annotation { "Feature Type Name" : "Feature", "Feature Type Description" : "" }
export const myFeature = defineFeature(function(context is Context, id is Id, definition is map)
    precondition{}
    {
        {
            var Q0;
            Q0=qCreatedBy(makeId("Top.planeOp"),FACE);
            var sketch = newSketch(context, id + "F0", { "sketchPlane" : qUnion([Q0])});
            skCircle(sketch, "E0", {"center": v(0, 0) * mm, "radius": 50 * mm});
            skSolve(sketch);
        }
        {
            var Q0;
            Q0=makeQuery(id+"F0.imprint","IMPRINT",FACE,{"disambiguationData":[TD([[makeQuery(id+"F0.imprint","IMPRINT",EDGE,{"derivedFrom":sQuery(id+"F0.wireOp",EDGE,"E0")}),1.0]])]});
            extrude(context, id + "F1", {"entities" : qUnion([Q0]), "depth" : 10 * mm});
        }
        {
            var Q0;
            Q0=makeQuery(id+"F1.opExtrude","SWEPT_FACE",FACE,{"disambiguationData":[OSD([sQuery(id+"F0.wireOp",EDGE,"E0")])]});
            var Q1;
            Q1=makeQuery(id+"F1.opExtrude","CAP_FACE",FACE,{"disambiguationData":[OSD([sQuery(id+"F0.wireOp",EDGE,"E0")])],"isStart":true});
            fillet(context, id + "F2", {"entities" : qUnion([Q0, Q1]), "radius" : 2 * mm, "tangentPropagation" : true, "allowEdgeOverflow" : false});
        }
        {
            var Q0;
            Q0=qCreatedBy(makeId("Top.planeOp"),FACE);
            var sketch = newSketch(context, id + "F3", { "sketchPlane" : qUnion([Q0])});
            skArc(sketch, "E1", {"start": v(45.47, 63.4) * mm, "mid": v(37.47, 55.4) * mm, "end": v(45.47, 47.4) * mm});
            skLineSegment(sketch, "E2", {"start": v(45.47, 55.4) * mm, "end": v(45.47, 63.4) * mm});
            skLineSegment(sketch, "E3", {"start": v(45.47, 63.4) * mm, "end": v(45.47, 47.4) * mm});
            skSolve(sketch);
        }
        {
            var Q0;
            {var subQ0=sQuery(id+"F3.wireOp",EDGE,"E1");Q0=makeQuery(id+"F3.imprint","IMPRINT",FACE,{"disambiguationData":[TD([[makeQuery(id+"F3.imprint","IMPRINT",EDGE,{"derivedFrom":subQ0}),1.0]])]});}
            var Q1;
            Q1=sQuery(id+"F3.wireOp",EDGE,"E3");
            revolve(context, id + "F4", {"entities" : qUnion([Q0]), "axis" : qUnion([Q1]), "revolveType" : RevolveType.FULL});
        }
        {
            var Q0;
            Q0=makeQuery(id+"F4.opRevolve","SWEPT_BODY",BODY,{"disambiguationData":[OSD([sQuery(id+"F3.wireOp",EDGE,"E1"),sQuery(id+"F3.wireOp",EDGE,"E3")])]});
            var Q1;
            Q1=makeQuery(id+"F4.opRevolve","SWEPT_FACE",FACE,{"disambiguationData":[OSD([sQuery(id+"F3.wireOp",EDGE,"E1")])]});
            transform(context, id + "F5", {"entities" : qUnion([Q0]), "transformType" : TransformType.TRANSLATION_3D, "dx" : -7.8 * mm, "dy" : 33.7 * mm, "dz" : 0 * mm, "makeCopy" : false});
        }
        {
            var Q0;
            Q0=qCreatedBy(makeId("Front.planeOp"),FACE);
            var sketch = newSketch(context, id + "F6", { "sketchPlane" : qUnion([Q0])});
            skLineSegment(sketch, "E4", {"start": v(0, 17.62) * mm, "end": v(49.25, 17.62) * mm});
            skLineSegment(sketch, "E5", {"start": v(49.25, 17.62) * mm, "end": v(23.09, 115.37) * mm});
            skLineSegment(sketch, "E6", {"start": v(23.09, 115.37) * mm, "end": v(0, 115.37) * mm});
            skLineSegment(sketch, "E7", {"start": v(0, 115.37) * mm, "end": v(0, 17.62) * mm});
            skLineSegment(sketch, "E8", {"start": v(44.4, 17.62) * mm, "end": v(18.23, 115.37) * mm});
            skSolve(sketch);
        }
        {
            var Q0;
            {var subQ0=sQuery(id+"F6.wireOp",EDGE,"E5");Q0=makeQuery(id+"F6.imprint","IMPRINT",FACE,{"disambiguationData":[TD([[makeQuery(id+"F6.imprint","IMPRINT",EDGE,{"derivedFrom":subQ0}),1.0]])]});}
            var Q1;
            Q1=sQuery(id+"F6.wireOp",EDGE,"E7");
            revolve(context, id + "F7", {"entities" : qUnion([Q0]), "axis" : qUnion([Q1]), "revolveType" : RevolveType.FULL});
        }
        {
            var Q0;
            Q0=makeQuery(id+"F7.opRevolve","SWEPT_BODY",BODY,{"disambiguationData":[OSD([sQuery(id+"F6.wireOp",EDGE,"E4"),sQuery(id+"F6.wireOp",EDGE,"E5"),sQuery(id+"F6.wireOp",EDGE,"E6"),sQuery(id+"F6.wireOp",EDGE,"E8")])]});
            transform(context, id + "F8", {"entities" : qUnion([Q0]), "transformType" : TransformType.TRANSLATION_3D, "dx" : 0 * mm, "dy" : 0 * mm, "dz" : -8.2 * mm, "makeCopy" : false});
        }
        {
            var Q0;
            Q0=makeQuery(id+"F4.opRevolve","SWEPT_BODY",BODY,{"disambiguationData":[OSD([sQuery(id+"F3.wireOp",EDGE,"E1"),sQuery(id+"F3.wireOp",EDGE,"E3")])]});
            transform(context, id + "F9", {"entities" : qUnion([Q0]), "transformType" : TransformType.TRANSLATION_3D, "dx" : -73 * mm, "dy" : 0 * mm, "dz" : 0 * mm, "makeCopy" : true});
        }
        {
            var Q0;
            Q0=makeQuery(id+"F9.opPattern","COPY",BODY,{"derivedFrom":makeQuery(id+"F4.opRevolve","SWEPT_BODY",BODY,{"disambiguationData":[OSD([sQuery(id+"F3.wireOp",EDGE,"E1"),sQuery(id+"F3.wireOp",EDGE,"E3")])]}),"instanceName":"1"});
            transform(context, id + "F10", {"entities" : qUnion([Q0]), "transformType" : TransformType.TRANSLATION_3D, "dx" : 62 * mm, "dy" : 46 * mm, "dz" : 0 * mm, "makeCopy" : true});
        }
        {
            var Q0;
            Q0=makeQuery(id+"F9.opPattern","COPY",BODY,{"derivedFrom":makeQuery(id+"F4.opRevolve","SWEPT_BODY",BODY,{"disambiguationData":[OSD([sQuery(id+"F3.wireOp",EDGE,"E1"),sQuery(id+"F3.wireOp",EDGE,"E3")])]}),"instanceName":"1"});
            var Q1;
            Q1=makeQuery(id+"F4.opRevolve","SWEPT_BODY",BODY,{"disambiguationData":[OSD([sQuery(id+"F3.wireOp",EDGE,"E1"),sQuery(id+"F3.wireOp",EDGE,"E3")])]});
            transform(context, id + "F11", {"entities" : qUnion([Q0, Q1]), "transformType" : TransformType.TRANSLATION_3D, "dx" : 29 * mm, "dy" : -104 * mm, "dz" : 31 * mm, "makeCopy" : false});
        }
        {
            var Q0;
            Q0=makeQuery(id+"F4.opRevolve","SWEPT_BODY",BODY,{"disambiguationData":[OSD([sQuery(id+"F3.wireOp",EDGE,"E1"),sQuery(id+"F3.wireOp",EDGE,"E3")])]});
            transform(context, id + "F12", {"entities" : qUnion([Q0]), "transformType" : TransformType.TRANSLATION_3D, "dx" : -53 * mm, "dy" : 4 * mm, "dz" : 25 * mm, "makeCopy" : false});
        }
        {
            var Q0;
            Q0=makeQuery(id+"F10.opPattern","COPY",BODY,{"derivedFrom":makeQuery(id+"F9.opPattern","COPY",BODY,{"derivedFrom":makeQuery(id+"F4.opRevolve","SWEPT_BODY",BODY,{"disambiguationData":[OSD([sQuery(id+"F3.wireOp",EDGE,"E1"),sQuery(id+"F3.wireOp",EDGE,"E3")])]}),"instanceName":"1"}),"instanceName":"1"});
            transform(context, id + "F13", {"entities" : qUnion([Q0]), "transformType" : TransformType.TRANSLATION_3D, "dx" : -36 * mm, "dy" : -122 * mm, "dz" : 77 * mm, "makeCopy" : false});
        }
        {
            var Q0;
            Q0=qCreatedBy(makeId("Front.planeOp"),FACE);
            var sketch = newSketch(context, id + "F14", { "sketchPlane" : qUnion([Q0])});
            skText(sketch, "E9", { "text": "Tutorial", "fontName": "OpenSans-Regular.ttf"});
            skText(sketch, "E10", { "text": "Kinematics", "fontName": "OpenSans-Regular.ttf"});
            skText(sketch, "E11", { "text": "Particle Physics", "fontName": "OpenSans-Regular.ttf"});
            const initialGuessF14  = {"E9": [-0.02165, 0.0885, 1, 0, 0.00375], "E10": [0.00114, 0.0665, 1, 0, 0.004], "E11": [-0.0259, 0.04173, 1, 0, 0.00358]};
            skSetInitialGuess(sketch, initialGuessF14);
            skSolve(sketch);
        }
        {
            var Q0;
            Q0 = qSketchRegion(id + "F14", true);
            extrude(context, id + "F15", {"entities" : qUnion([Q0]), "depth" : 2 * mm});
        }
        {
            var Q0;
            Q0=makeQuery(id+"F15.opExtrude","SWEPT_BODY",BODY,{"disambiguationData":[OSD([sQuery(id+"F14.wireOp",EDGE,"E9.sketch_text.stroke-0"),sQuery(id+"F14.wireOp",EDGE,"E9.sketch_text.stroke-1"),sQuery(id+"F14.wireOp",EDGE,"E9.sketch_text.stroke-2"),sQuery(id+"F14.wireOp",EDGE,"E9.sketch_text.stroke-3"),sQuery(id+"F14.wireOp",EDGE,"E9.sketch_text.stroke-4"),sQuery(id+"F14.wireOp",EDGE,"E9.sketch_text.stroke-5"),sQuery(id+"F14.wireOp",EDGE,"E9.sketch_text.stroke-6"),sQuery(id+"F14.wireOp",EDGE,"E9.sketch_text.stroke-7"),sQuery(id+"F14.wireOp",EDGE,"E9.sketch_text.stroke-8"),sQuery(id+"F14.wireOp",EDGE,"E9.sketch_text.stroke-9"),sQuery(id+"F14.wireOp",EDGE,"E9.sketch_text.stroke-10"),sQuery(id+"F14.wireOp",EDGE,"E9.sketch_text.stroke-11"),sQuery(id+"F14.wireOp",EDGE,"E9.sketch_text.stroke-12")])]});
            var Q1;
            Q1=makeQuery(id+"F15.opExtrude","SWEPT_BODY",BODY,{"disambiguationData":[OSD([sQuery(id+"F14.wireOp",EDGE,"E9.sketch_text.stroke-13"),sQuery(id+"F14.wireOp",EDGE,"E9.sketch_text.stroke-14"),sQuery(id+"F14.wireOp",EDGE,"E9.sketch_text.stroke-15"),sQuery(id+"F14.wireOp",EDGE,"E9.sketch_text.stroke-16"),sQuery(id+"F14.wireOp",EDGE,"E9.sketch_text.stroke-17"),sQuery(id+"F14.wireOp",EDGE,"E9.sketch_text.stroke-18"),sQuery(id+"F14.wireOp",EDGE,"E9.sketch_text.stroke-19"),sQuery(id+"F14.wireOp",EDGE,"E9.sketch_text.stroke-20"),sQuery(id+"F14.wireOp",EDGE,"E9.sketch_text.stroke-21"),sQuery(id+"F14.wireOp",EDGE,"E9.sketch_text.stroke-22"),sQuery(id+"F14.wireOp",EDGE,"E9.sketch_text.stroke-23"),sQuery(id+"F14.wireOp",EDGE,"E9.sketch_text.stroke-24"),sQuery(id+"F14.wireOp",EDGE,"E9.sketch_text.stroke-25"),sQuery(id+"F14.wireOp",EDGE,"E9.sketch_text.stroke-26"),sQuery(id+"F14.wireOp",EDGE,"E9.sketch_text.stroke-27"),sQuery(id+"F14.wireOp",EDGE,"E9.sketch_text.stroke-28"),sQuery(id+"F14.wireOp",EDGE,"E9.sketch_text.stroke-29"),sQuery(id+"F14.wireOp",EDGE,"E9.sketch_text.stroke-30"),sQuery(id+"F14.wireOp",EDGE,"E9.sketch_text.stroke-31"),sQuery(id+"F14.wireOp",EDGE,"E9.sketch_text.stroke-32"),sQuery(id+"F14.wireOp",EDGE,"E9.sketch_text.stroke-33"),sQuery(id+"F14.wireOp",EDGE,"E9.sketch_text.stroke-34"),sQuery(id+"F14.wireOp",EDGE,"E9.sketch_text.stroke-35"),sQuery(id+"F14.wireOp",EDGE,"E9.sketch_text.stroke-36"),sQuery(id+"F14.wireOp",EDGE,"E9.sketch_text.stroke-37")])]});
            var Q2;
            Q2=makeQuery(id+"F15.opExtrude","SWEPT_BODY",BODY,{"disambiguationData":[OSD([sQuery(id+"F14.wireOp",EDGE,"E9.sketch_text.stroke-38"),sQuery(id+"F14.wireOp",EDGE,"E9.sketch_text.stroke-39"),sQuery(id+"F14.wireOp",EDGE,"E9.sketch_text.stroke-40"),sQuery(id+"F14.wireOp",EDGE,"E9.sketch_text.stroke-41"),sQuery(id+"F14.wireOp",EDGE,"E9.sketch_text.stroke-42"),sQuery(id+"F14.wireOp",EDGE,"E9.sketch_text.stroke-43"),sQuery(id+"F14.wireOp",EDGE,"E9.sketch_text.stroke-44"),sQuery(id+"F14.wireOp",EDGE,"E9.sketch_text.stroke-45"),sQuery(id+"F14.wireOp",EDGE,"E9.sketch_text.stroke-46"),sQuery(id+"F14.wireOp",EDGE,"E9.sketch_text.stroke-47"),sQuery(id+"F14.wireOp",EDGE,"E9.sketch_text.stroke-48"),sQuery(id+"F14.wireOp",EDGE,"E9.sketch_text.stroke-49"),sQuery(id+"F14.wireOp",EDGE,"E9.sketch_text.stroke-50"),sQuery(id+"F14.wireOp",EDGE,"E9.sketch_text.stroke-51"),sQuery(id+"F14.wireOp",EDGE,"E9.sketch_text.stroke-52"),sQuery(id+"F14.wireOp",EDGE,"E9.sketch_text.stroke-53"),sQuery(id+"F14.wireOp",EDGE,"E9.sketch_text.stroke-54"),sQuery(id+"F14.wireOp",EDGE,"E9.sketch_text.stroke-55"),sQuery(id+"F14.wireOp",EDGE,"E9.sketch_text.stroke-56")])]});
            var Q3;
            Q3=makeQuery(id+"F15.opExtrude","SWEPT_BODY",BODY,{"disambiguationData":[OSD([sQuery(id+"F14.wireOp",EDGE,"E9.sketch_text.stroke-57"),sQuery(id+"F14.wireOp",EDGE,"E9.sketch_text.stroke-58"),sQuery(id+"F14.wireOp",EDGE,"E9.sketch_text.stroke-59"),sQuery(id+"F14.wireOp",EDGE,"E9.sketch_text.stroke-60"),sQuery(id+"F14.wireOp",EDGE,"E9.sketch_text.stroke-61"),sQuery(id+"F14.wireOp",EDGE,"E9.sketch_text.stroke-62"),sQuery(id+"F14.wireOp",EDGE,"E9.sketch_text.stroke-63"),sQuery(id+"F14.wireOp",EDGE,"E9.sketch_text.stroke-64"),sQuery(id+"F14.wireOp",EDGE,"E9.sketch_text.stroke-65"),sQuery(id+"F14.wireOp",EDGE,"E9.sketch_text.stroke-66"),sQuery(id+"F14.wireOp",EDGE,"E9.sketch_text.stroke-67"),sQuery(id+"F14.wireOp",EDGE,"E9.sketch_text.stroke-68"),sQuery(id+"F14.wireOp",EDGE,"E9.sketch_text.stroke-69")])]});
            var Q4;
            Q4=makeQuery(id+"F15.opExtrude","SWEPT_BODY",BODY,{"disambiguationData":[OSD([sQuery(id+"F14.wireOp",EDGE,"E9.sketch_text.stroke-70"),sQuery(id+"F14.wireOp",EDGE,"E9.sketch_text.stroke-71"),sQuery(id+"F14.wireOp",EDGE,"E9.sketch_text.stroke-72"),sQuery(id+"F14.wireOp",EDGE,"E9.sketch_text.stroke-73"),sQuery(id+"F14.wireOp",EDGE,"E9.sketch_text.stroke-74"),sQuery(id+"F14.wireOp",EDGE,"E9.sketch_text.stroke-75"),sQuery(id+"F14.wireOp",EDGE,"E9.sketch_text.stroke-76"),sQuery(id+"F14.wireOp",EDGE,"E9.sketch_text.stroke-77"),sQuery(id+"F14.wireOp",EDGE,"E9.sketch_text.stroke-78"),sQuery(id+"F14.wireOp",EDGE,"E9.sketch_text.stroke-79"),sQuery(id+"F14.wireOp",EDGE,"E9.sketch_text.stroke-80"),sQuery(id+"F14.wireOp",EDGE,"E9.sketch_text.stroke-81"),sQuery(id+"F14.wireOp",EDGE,"E9.sketch_text.stroke-82"),sQuery(id+"F14.wireOp",EDGE,"E9.sketch_text.stroke-83"),sQuery(id+"F14.wireOp",EDGE,"E9.sketch_text.stroke-84"),sQuery(id+"F14.wireOp",EDGE,"E9.sketch_text.stroke-85"),sQuery(id+"F14.wireOp",EDGE,"E9.sketch_text.stroke-86")])]});
            var Q5;
            Q5=makeQuery(id+"F15.opExtrude","SWEPT_BODY",BODY,{"disambiguationData":[OSD([sQuery(id+"F14.wireOp",EDGE,"E9.sketch_text.stroke-87"),sQuery(id+"F14.wireOp",EDGE,"E9.sketch_text.stroke-88"),sQuery(id+"F14.wireOp",EDGE,"E9.sketch_text.stroke-89"),sQuery(id+"F14.wireOp",EDGE,"E9.sketch_text.stroke-90"),sQuery(id+"F14.wireOp",EDGE,"E9.sketch_text.stroke-91"),sQuery(id+"F14.wireOp",EDGE,"E9.sketch_text.stroke-92"),sQuery(id+"F14.wireOp",EDGE,"E9.sketch_text.stroke-93"),sQuery(id+"F14.wireOp",EDGE,"E9.sketch_text.stroke-94"),sQuery(id+"F14.wireOp",EDGE,"E9.sketch_text.stroke-95"),sQuery(id+"F14.wireOp",EDGE,"E9.sketch_text.stroke-96"),sQuery(id+"F14.wireOp",EDGE,"E9.sketch_text.stroke-97"),sQuery(id+"F14.wireOp",EDGE,"E9.sketch_text.stroke-98"),sQuery(id+"F14.wireOp",EDGE,"E9.sketch_text.stroke-99"),sQuery(id+"F14.wireOp",EDGE,"E9.sketch_text.stroke-100"),sQuery(id+"F14.wireOp",EDGE,"E9.sketch_text.stroke-101"),sQuery(id+"F14.wireOp",EDGE,"E9.sketch_text.stroke-102"),sQuery(id+"F14.wireOp",EDGE,"E9.sketch_text.stroke-103")])]});
            var Q6;
            Q6=makeQuery(id+"F15.opExtrude","SWEPT_BODY",BODY,{"disambiguationData":[OSD([sQuery(id+"F14.wireOp",EDGE,"E9.sketch_text.stroke-104"),sQuery(id+"F14.wireOp",EDGE,"E9.sketch_text.stroke-105"),sQuery(id+"F14.wireOp",EDGE,"E9.sketch_text.stroke-106"),sQuery(id+"F14.wireOp",EDGE,"E9.sketch_text.stroke-107"),sQuery(id+"F14.wireOp",EDGE,"E9.sketch_text.stroke-108"),sQuery(id+"F14.wireOp",EDGE,"E9.sketch_text.stroke-109"),sQuery(id+"F14.wireOp",EDGE,"E9.sketch_text.stroke-110"),sQuery(id+"F14.wireOp",EDGE,"E9.sketch_text.stroke-111"),sQuery(id+"F14.wireOp",EDGE,"E9.sketch_text.stroke-112"),sQuery(id+"F14.wireOp",EDGE,"E9.sketch_text.stroke-113"),sQuery(id+"F14.wireOp",EDGE,"E9.sketch_text.stroke-114"),sQuery(id+"F14.wireOp",EDGE,"E9.sketch_text.stroke-115"),sQuery(id+"F14.wireOp",EDGE,"E9.sketch_text.stroke-116"),sQuery(id+"F14.wireOp",EDGE,"E9.sketch_text.stroke-117"),sQuery(id+"F14.wireOp",EDGE,"E9.sketch_text.stroke-118"),sQuery(id+"F14.wireOp",EDGE,"E9.sketch_text.stroke-119"),sQuery(id+"F14.wireOp",EDGE,"E9.sketch_text.stroke-120")])]});
            var Q7;
            Q7=makeQuery(id+"F15.opExtrude","SWEPT_BODY",BODY,{"disambiguationData":[OSD([sQuery(id+"F14.wireOp",EDGE,"E9.sketch_text.stroke-121"),sQuery(id+"F14.wireOp",EDGE,"E9.sketch_text.stroke-122"),sQuery(id+"F14.wireOp",EDGE,"E9.sketch_text.stroke-123"),sQuery(id+"F14.wireOp",EDGE,"E9.sketch_text.stroke-124"),sQuery(id+"F14.wireOp",EDGE,"E9.sketch_text.stroke-125"),sQuery(id+"F14.wireOp",EDGE,"E9.sketch_text.stroke-126"),sQuery(id+"F14.wireOp",EDGE,"E9.sketch_text.stroke-127"),sQuery(id+"F14.wireOp",EDGE,"E9.sketch_text.stroke-128"),sQuery(id+"F14.wireOp",EDGE,"E9.sketch_text.stroke-129"),sQuery(id+"F14.wireOp",EDGE,"E9.sketch_text.stroke-130"),sQuery(id+"F14.wireOp",EDGE,"E9.sketch_text.stroke-131"),sQuery(id+"F14.wireOp",EDGE,"E9.sketch_text.stroke-132"),sQuery(id+"F14.wireOp",EDGE,"E9.sketch_text.stroke-133"),sQuery(id+"F14.wireOp",EDGE,"E9.sketch_text.stroke-134"),sQuery(id+"F14.wireOp",EDGE,"E9.sketch_text.stroke-135"),sQuery(id+"F14.wireOp",EDGE,"E9.sketch_text.stroke-136"),sQuery(id+"F14.wireOp",EDGE,"E9.sketch_text.stroke-137"),sQuery(id+"F14.wireOp",EDGE,"E9.sketch_text.stroke-138"),sQuery(id+"F14.wireOp",EDGE,"E9.sketch_text.stroke-139"),sQuery(id+"F14.wireOp",EDGE,"E9.sketch_text.stroke-140"),sQuery(id+"F14.wireOp",EDGE,"E9.sketch_text.stroke-141"),sQuery(id+"F14.wireOp",EDGE,"E9.sketch_text.stroke-142"),sQuery(id+"F14.wireOp",EDGE,"E9.sketch_text.stroke-143"),sQuery(id+"F14.wireOp",EDGE,"E9.sketch_text.stroke-144"),sQuery(id+"F14.wireOp",EDGE,"E9.sketch_text.stroke-145"),sQuery(id+"F14.wireOp",EDGE,"E9.sketch_text.stroke-146"),sQuery(id+"F14.wireOp",EDGE,"E9.sketch_text.stroke-147"),sQuery(id+"F14.wireOp",EDGE,"E9.sketch_text.stroke-148")])]});
            var Q8;
            Q8=makeQuery(id+"F15.opExtrude","SWEPT_BODY",BODY,{"disambiguationData":[OSD([sQuery(id+"F14.wireOp",EDGE,"E9.sketch_text.stroke-149"),sQuery(id+"F14.wireOp",EDGE,"E9.sketch_text.stroke-150"),sQuery(id+"F14.wireOp",EDGE,"E9.sketch_text.stroke-151"),sQuery(id+"F14.wireOp",EDGE,"E9.sketch_text.stroke-152"),sQuery(id+"F14.wireOp",EDGE,"E9.sketch_text.stroke-153"),sQuery(id+"F14.wireOp",EDGE,"E9.sketch_text.stroke-154"),sQuery(id+"F14.wireOp",EDGE,"E9.sketch_text.stroke-155"),sQuery(id+"F14.wireOp",EDGE,"E9.sketch_text.stroke-156"),sQuery(id+"F14.wireOp",EDGE,"E9.sketch_text.stroke-157"),sQuery(id+"F14.wireOp",EDGE,"E9.sketch_text.stroke-158"),sQuery(id+"F14.wireOp",EDGE,"E9.sketch_text.stroke-159"),sQuery(id+"F14.wireOp",EDGE,"E9.sketch_text.stroke-160"),sQuery(id+"F14.wireOp",EDGE,"E9.sketch_text.stroke-161"),sQuery(id+"F14.wireOp",EDGE,"E9.sketch_text.stroke-162"),sQuery(id+"F14.wireOp",EDGE,"E9.sketch_text.stroke-163"),sQuery(id+"F14.wireOp",EDGE,"E9.sketch_text.stroke-164")])]});
            transform(context, id + "F16", {"entities" : qUnion([Q0, Q1, Q2, Q3, Q4, Q5, Q6, Q7, Q8]), "transformType" : TransformType.TRANSLATION_3D, "dx" : 0.4 * mm, "dy" : 14.2 * mm, "dz" : -1.1 * mm, "makeCopy" : false});
        }
        {
            var Q0;
            Q0=makeQuery(id+"F15.opExtrude","SWEPT_BODY",BODY,{"disambiguationData":[OSD([sQuery(id+"F14.wireOp",EDGE,"E10.sketch_text.stroke-0"),sQuery(id+"F14.wireOp",EDGE,"E10.sketch_text.stroke-1"),sQuery(id+"F14.wireOp",EDGE,"E10.sketch_text.stroke-2"),sQuery(id+"F14.wireOp",EDGE,"E10.sketch_text.stroke-3"),sQuery(id+"F14.wireOp",EDGE,"E10.sketch_text.stroke-4"),sQuery(id+"F14.wireOp",EDGE,"E10.sketch_text.stroke-5"),sQuery(id+"F14.wireOp",EDGE,"E10.sketch_text.stroke-6"),sQuery(id+"F14.wireOp",EDGE,"E10.sketch_text.stroke-7"),sQuery(id+"F14.wireOp",EDGE,"E10.sketch_text.stroke-8"),sQuery(id+"F14.wireOp",EDGE,"E10.sketch_text.stroke-9"),sQuery(id+"F14.wireOp",EDGE,"E10.sketch_text.stroke-10"),sQuery(id+"F14.wireOp",EDGE,"E10.sketch_text.stroke-11")])]});
            var Q1;
            Q1=makeQuery(id+"F15.opExtrude","SWEPT_BODY",BODY,{"disambiguationData":[OSD([sQuery(id+"F14.wireOp",EDGE,"E10.sketch_text.stroke-12"),sQuery(id+"F14.wireOp",EDGE,"E10.sketch_text.stroke-13"),sQuery(id+"F14.wireOp",EDGE,"E10.sketch_text.stroke-14"),sQuery(id+"F14.wireOp",EDGE,"E10.sketch_text.stroke-15")])]});
            var Q2;
            Q2=makeQuery(id+"F15.opExtrude","SWEPT_BODY",BODY,{"disambiguationData":[OSD([sQuery(id+"F14.wireOp",EDGE,"E10.sketch_text.stroke-16"),sQuery(id+"F14.wireOp",EDGE,"E10.sketch_text.stroke-17"),sQuery(id+"F14.wireOp",EDGE,"E10.sketch_text.stroke-18"),sQuery(id+"F14.wireOp",EDGE,"E10.sketch_text.stroke-19"),sQuery(id+"F14.wireOp",EDGE,"E10.sketch_text.stroke-20"),sQuery(id+"F14.wireOp",EDGE,"E10.sketch_text.stroke-21"),sQuery(id+"F14.wireOp",EDGE,"E10.sketch_text.stroke-22"),sQuery(id+"F14.wireOp",EDGE,"E10.sketch_text.stroke-23")])]});
            var Q3;
            Q3=makeQuery(id+"F15.opExtrude","SWEPT_BODY",BODY,{"disambiguationData":[OSD([sQuery(id+"F14.wireOp",EDGE,"E10.sketch_text.stroke-24"),sQuery(id+"F14.wireOp",EDGE,"E10.sketch_text.stroke-25"),sQuery(id+"F14.wireOp",EDGE,"E10.sketch_text.stroke-26"),sQuery(id+"F14.wireOp",EDGE,"E10.sketch_text.stroke-27"),sQuery(id+"F14.wireOp",EDGE,"E10.sketch_text.stroke-28"),sQuery(id+"F14.wireOp",EDGE,"E10.sketch_text.stroke-29"),sQuery(id+"F14.wireOp",EDGE,"E10.sketch_text.stroke-30"),sQuery(id+"F14.wireOp",EDGE,"E10.sketch_text.stroke-31"),sQuery(id+"F14.wireOp",EDGE,"E10.sketch_text.stroke-32"),sQuery(id+"F14.wireOp",EDGE,"E10.sketch_text.stroke-33"),sQuery(id+"F14.wireOp",EDGE,"E10.sketch_text.stroke-34"),sQuery(id+"F14.wireOp",EDGE,"E10.sketch_text.stroke-35"),sQuery(id+"F14.wireOp",EDGE,"E10.sketch_text.stroke-36"),sQuery(id+"F14.wireOp",EDGE,"E10.sketch_text.stroke-37"),sQuery(id+"F14.wireOp",EDGE,"E10.sketch_text.stroke-38"),sQuery(id+"F14.wireOp",EDGE,"E10.sketch_text.stroke-39"),sQuery(id+"F14.wireOp",EDGE,"E10.sketch_text.stroke-40")])]});
            var Q4;
            Q4=makeQuery(id+"F15.opExtrude","SWEPT_BODY",BODY,{"disambiguationData":[OSD([sQuery(id+"F14.wireOp",EDGE,"E10.sketch_text.stroke-41"),sQuery(id+"F14.wireOp",EDGE,"E10.sketch_text.stroke-42"),sQuery(id+"F14.wireOp",EDGE,"E10.sketch_text.stroke-43"),sQuery(id+"F14.wireOp",EDGE,"E10.sketch_text.stroke-44"),sQuery(id+"F14.wireOp",EDGE,"E10.sketch_text.stroke-45"),sQuery(id+"F14.wireOp",EDGE,"E10.sketch_text.stroke-46"),sQuery(id+"F14.wireOp",EDGE,"E10.sketch_text.stroke-47"),sQuery(id+"F14.wireOp",EDGE,"E10.sketch_text.stroke-48"),sQuery(id+"F14.wireOp",EDGE,"E10.sketch_text.stroke-49"),sQuery(id+"F14.wireOp",EDGE,"E10.sketch_text.stroke-50"),sQuery(id+"F14.wireOp",EDGE,"E10.sketch_text.stroke-51"),sQuery(id+"F14.wireOp",EDGE,"E10.sketch_text.stroke-52"),sQuery(id+"F14.wireOp",EDGE,"E10.sketch_text.stroke-53"),sQuery(id+"F14.wireOp",EDGE,"E10.sketch_text.stroke-54"),sQuery(id+"F14.wireOp",EDGE,"E10.sketch_text.stroke-55"),sQuery(id+"F14.wireOp",EDGE,"E10.sketch_text.stroke-56"),sQuery(id+"F14.wireOp",EDGE,"E10.sketch_text.stroke-57"),sQuery(id+"F14.wireOp",EDGE,"E10.sketch_text.stroke-58"),sQuery(id+"F14.wireOp",EDGE,"E10.sketch_text.stroke-59")])]});
            var Q5;
            Q5=makeQuery(id+"F15.opExtrude","SWEPT_BODY",BODY,{"disambiguationData":[OSD([sQuery(id+"F14.wireOp",EDGE,"E10.sketch_text.stroke-60"),sQuery(id+"F14.wireOp",EDGE,"E10.sketch_text.stroke-61"),sQuery(id+"F14.wireOp",EDGE,"E10.sketch_text.stroke-62"),sQuery(id+"F14.wireOp",EDGE,"E10.sketch_text.stroke-63"),sQuery(id+"F14.wireOp",EDGE,"E10.sketch_text.stroke-64"),sQuery(id+"F14.wireOp",EDGE,"E10.sketch_text.stroke-65"),sQuery(id+"F14.wireOp",EDGE,"E10.sketch_text.stroke-66"),sQuery(id+"F14.wireOp",EDGE,"E10.sketch_text.stroke-67"),sQuery(id+"F14.wireOp",EDGE,"E10.sketch_text.stroke-68"),sQuery(id+"F14.wireOp",EDGE,"E10.sketch_text.stroke-69"),sQuery(id+"F14.wireOp",EDGE,"E10.sketch_text.stroke-70"),sQuery(id+"F14.wireOp",EDGE,"E10.sketch_text.stroke-71"),sQuery(id+"F14.wireOp",EDGE,"E10.sketch_text.stroke-72"),sQuery(id+"F14.wireOp",EDGE,"E10.sketch_text.stroke-73"),sQuery(id+"F14.wireOp",EDGE,"E10.sketch_text.stroke-74"),sQuery(id+"F14.wireOp",EDGE,"E10.sketch_text.stroke-75"),sQuery(id+"F14.wireOp",EDGE,"E10.sketch_text.stroke-76"),sQuery(id+"F14.wireOp",EDGE,"E10.sketch_text.stroke-77"),sQuery(id+"F14.wireOp",EDGE,"E10.sketch_text.stroke-78"),sQuery(id+"F14.wireOp",EDGE,"E10.sketch_text.stroke-79"),sQuery(id+"F14.wireOp",EDGE,"E10.sketch_text.stroke-80"),sQuery(id+"F14.wireOp",EDGE,"E10.sketch_text.stroke-81"),sQuery(id+"F14.wireOp",EDGE,"E10.sketch_text.stroke-82"),sQuery(id+"F14.wireOp",EDGE,"E10.sketch_text.stroke-83"),sQuery(id+"F14.wireOp",EDGE,"E10.sketch_text.stroke-84"),sQuery(id+"F14.wireOp",EDGE,"E10.sketch_text.stroke-85"),sQuery(id+"F14.wireOp",EDGE,"E10.sketch_text.stroke-86"),sQuery(id+"F14.wireOp",EDGE,"E10.sketch_text.stroke-87")])]});
            var Q6;
            Q6=makeQuery(id+"F15.opExtrude","SWEPT_BODY",BODY,{"disambiguationData":[OSD([sQuery(id+"F14.wireOp",EDGE,"E10.sketch_text.stroke-88"),sQuery(id+"F14.wireOp",EDGE,"E10.sketch_text.stroke-89"),sQuery(id+"F14.wireOp",EDGE,"E10.sketch_text.stroke-90"),sQuery(id+"F14.wireOp",EDGE,"E10.sketch_text.stroke-91"),sQuery(id+"F14.wireOp",EDGE,"E10.sketch_text.stroke-92"),sQuery(id+"F14.wireOp",EDGE,"E10.sketch_text.stroke-93"),sQuery(id+"F14.wireOp",EDGE,"E10.sketch_text.stroke-94"),sQuery(id+"F14.wireOp",EDGE,"E10.sketch_text.stroke-95"),sQuery(id+"F14.wireOp",EDGE,"E10.sketch_text.stroke-96"),sQuery(id+"F14.wireOp",EDGE,"E10.sketch_text.stroke-97"),sQuery(id+"F14.wireOp",EDGE,"E10.sketch_text.stroke-98"),sQuery(id+"F14.wireOp",EDGE,"E10.sketch_text.stroke-99"),sQuery(id+"F14.wireOp",EDGE,"E10.sketch_text.stroke-100"),sQuery(id+"F14.wireOp",EDGE,"E10.sketch_text.stroke-101"),sQuery(id+"F14.wireOp",EDGE,"E10.sketch_text.stroke-102"),sQuery(id+"F14.wireOp",EDGE,"E10.sketch_text.stroke-103"),sQuery(id+"F14.wireOp",EDGE,"E10.sketch_text.stroke-104"),sQuery(id+"F14.wireOp",EDGE,"E10.sketch_text.stroke-105"),sQuery(id+"F14.wireOp",EDGE,"E10.sketch_text.stroke-106"),sQuery(id+"F14.wireOp",EDGE,"E10.sketch_text.stroke-107"),sQuery(id+"F14.wireOp",EDGE,"E10.sketch_text.stroke-108"),sQuery(id+"F14.wireOp",EDGE,"E10.sketch_text.stroke-109"),sQuery(id+"F14.wireOp",EDGE,"E10.sketch_text.stroke-110"),sQuery(id+"F14.wireOp",EDGE,"E10.sketch_text.stroke-111"),sQuery(id+"F14.wireOp",EDGE,"E10.sketch_text.stroke-112"),sQuery(id+"F14.wireOp",EDGE,"E10.sketch_text.stroke-113"),sQuery(id+"F14.wireOp",EDGE,"E10.sketch_text.stroke-114")])]});
            var Q7;
            Q7=makeQuery(id+"F15.opExtrude","SWEPT_BODY",BODY,{"disambiguationData":[OSD([sQuery(id+"F14.wireOp",EDGE,"E10.sketch_text.stroke-115"),sQuery(id+"F14.wireOp",EDGE,"E10.sketch_text.stroke-116"),sQuery(id+"F14.wireOp",EDGE,"E10.sketch_text.stroke-117"),sQuery(id+"F14.wireOp",EDGE,"E10.sketch_text.stroke-118"),sQuery(id+"F14.wireOp",EDGE,"E10.sketch_text.stroke-119"),sQuery(id+"F14.wireOp",EDGE,"E10.sketch_text.stroke-120"),sQuery(id+"F14.wireOp",EDGE,"E10.sketch_text.stroke-121"),sQuery(id+"F14.wireOp",EDGE,"E10.sketch_text.stroke-122"),sQuery(id+"F14.wireOp",EDGE,"E10.sketch_text.stroke-123"),sQuery(id+"F14.wireOp",EDGE,"E10.sketch_text.stroke-124"),sQuery(id+"F14.wireOp",EDGE,"E10.sketch_text.stroke-125"),sQuery(id+"F14.wireOp",EDGE,"E10.sketch_text.stroke-126"),sQuery(id+"F14.wireOp",EDGE,"E10.sketch_text.stroke-127"),sQuery(id+"F14.wireOp",EDGE,"E10.sketch_text.stroke-128"),sQuery(id+"F14.wireOp",EDGE,"E10.sketch_text.stroke-129"),sQuery(id+"F14.wireOp",EDGE,"E10.sketch_text.stroke-130"),sQuery(id+"F14.wireOp",EDGE,"E10.sketch_text.stroke-131"),sQuery(id+"F14.wireOp",EDGE,"E10.sketch_text.stroke-132"),sQuery(id+"F14.wireOp",EDGE,"E10.sketch_text.stroke-133")])]});
            var Q8;
            Q8=makeQuery(id+"F15.opExtrude","SWEPT_BODY",BODY,{"disambiguationData":[OSD([sQuery(id+"F14.wireOp",EDGE,"E10.sketch_text.stroke-134"),sQuery(id+"F14.wireOp",EDGE,"E10.sketch_text.stroke-135"),sQuery(id+"F14.wireOp",EDGE,"E10.sketch_text.stroke-136"),sQuery(id+"F14.wireOp",EDGE,"E10.sketch_text.stroke-137")])]});
            var Q9;
            Q9=makeQuery(id+"F15.opExtrude","SWEPT_BODY",BODY,{"disambiguationData":[OSD([sQuery(id+"F14.wireOp",EDGE,"E10.sketch_text.stroke-138"),sQuery(id+"F14.wireOp",EDGE,"E10.sketch_text.stroke-139"),sQuery(id+"F14.wireOp",EDGE,"E10.sketch_text.stroke-140"),sQuery(id+"F14.wireOp",EDGE,"E10.sketch_text.stroke-141"),sQuery(id+"F14.wireOp",EDGE,"E10.sketch_text.stroke-142"),sQuery(id+"F14.wireOp",EDGE,"E10.sketch_text.stroke-143"),sQuery(id+"F14.wireOp",EDGE,"E10.sketch_text.stroke-144"),sQuery(id+"F14.wireOp",EDGE,"E10.sketch_text.stroke-145")])]});
            var Q10;
            Q10=makeQuery(id+"F15.opExtrude","SWEPT_BODY",BODY,{"disambiguationData":[OSD([sQuery(id+"F14.wireOp",EDGE,"E10.sketch_text.stroke-146"),sQuery(id+"F14.wireOp",EDGE,"E10.sketch_text.stroke-147"),sQuery(id+"F14.wireOp",EDGE,"E10.sketch_text.stroke-148"),sQuery(id+"F14.wireOp",EDGE,"E10.sketch_text.stroke-149"),sQuery(id+"F14.wireOp",EDGE,"E10.sketch_text.stroke-150"),sQuery(id+"F14.wireOp",EDGE,"E10.sketch_text.stroke-151"),sQuery(id+"F14.wireOp",EDGE,"E10.sketch_text.stroke-152"),sQuery(id+"F14.wireOp",EDGE,"E10.sketch_text.stroke-153"),sQuery(id+"F14.wireOp",EDGE,"E10.sketch_text.stroke-154"),sQuery(id+"F14.wireOp",EDGE,"E10.sketch_text.stroke-155"),sQuery(id+"F14.wireOp",EDGE,"E10.sketch_text.stroke-156"),sQuery(id+"F14.wireOp",EDGE,"E10.sketch_text.stroke-157"),sQuery(id+"F14.wireOp",EDGE,"E10.sketch_text.stroke-158"),sQuery(id+"F14.wireOp",EDGE,"E10.sketch_text.stroke-159"),sQuery(id+"F14.wireOp",EDGE,"E10.sketch_text.stroke-160")])]});
            var Q11;
            Q11=makeQuery(id+"F15.opExtrude","SWEPT_BODY",BODY,{"disambiguationData":[OSD([sQuery(id+"F14.wireOp",EDGE,"E10.sketch_text.stroke-161"),sQuery(id+"F14.wireOp",EDGE,"E10.sketch_text.stroke-162"),sQuery(id+"F14.wireOp",EDGE,"E10.sketch_text.stroke-163"),sQuery(id+"F14.wireOp",EDGE,"E10.sketch_text.stroke-164"),sQuery(id+"F14.wireOp",EDGE,"E10.sketch_text.stroke-165"),sQuery(id+"F14.wireOp",EDGE,"E10.sketch_text.stroke-166"),sQuery(id+"F14.wireOp",EDGE,"E10.sketch_text.stroke-167"),sQuery(id+"F14.wireOp",EDGE,"E10.sketch_text.stroke-168"),sQuery(id+"F14.wireOp",EDGE,"E10.sketch_text.stroke-169"),sQuery(id+"F14.wireOp",EDGE,"E10.sketch_text.stroke-170"),sQuery(id+"F14.wireOp",EDGE,"E10.sketch_text.stroke-171"),sQuery(id+"F14.wireOp",EDGE,"E10.sketch_text.stroke-172"),sQuery(id+"F14.wireOp",EDGE,"E10.sketch_text.stroke-173"),sQuery(id+"F14.wireOp",EDGE,"E10.sketch_text.stroke-174"),sQuery(id+"F14.wireOp",EDGE,"E10.sketch_text.stroke-175"),sQuery(id+"F14.wireOp",EDGE,"E10.sketch_text.stroke-176"),sQuery(id+"F14.wireOp",EDGE,"E10.sketch_text.stroke-177"),sQuery(id+"F14.wireOp",EDGE,"E10.sketch_text.stroke-178"),sQuery(id+"F14.wireOp",EDGE,"E10.sketch_text.stroke-179"),sQuery(id+"F14.wireOp",EDGE,"E10.sketch_text.stroke-180"),sQuery(id+"F14.wireOp",EDGE,"E10.sketch_text.stroke-181"),sQuery(id+"F14.wireOp",EDGE,"E10.sketch_text.stroke-182"),sQuery(id+"F14.wireOp",EDGE,"E10.sketch_text.stroke-183"),sQuery(id+"F14.wireOp",EDGE,"E10.sketch_text.stroke-184"),sQuery(id+"F14.wireOp",EDGE,"E10.sketch_text.stroke-185")])]});
            transform(context, id + "F17", {"entities" : qUnion([Q0, Q1, Q2, Q3, Q4, Q5, Q6, Q7, Q8, Q9, Q10, Q11]), "transformType" : TransformType.TRANSLATION_3D, "dx" : 0 * mm, "dy" : -9.4 * mm, "dz" : 0 * mm, "makeCopy" : false});
        }
        {
            var Q0;
            Q0=makeQuery(id+"F15.opExtrude","SWEPT_BODY",BODY,{"disambiguationData":[OSD([sQuery(id+"F14.wireOp",EDGE,"E11.sketch_text.stroke-0"),sQuery(id+"F14.wireOp",EDGE,"E11.sketch_text.stroke-1"),sQuery(id+"F14.wireOp",EDGE,"E11.sketch_text.stroke-2"),sQuery(id+"F14.wireOp",EDGE,"E11.sketch_text.stroke-3"),sQuery(id+"F14.wireOp",EDGE,"E11.sketch_text.stroke-4"),sQuery(id+"F14.wireOp",EDGE,"E11.sketch_text.stroke-5"),sQuery(id+"F14.wireOp",EDGE,"E11.sketch_text.stroke-6"),sQuery(id+"F14.wireOp",EDGE,"E11.sketch_text.stroke-7"),sQuery(id+"F14.wireOp",EDGE,"E11.sketch_text.stroke-8"),sQuery(id+"F14.wireOp",EDGE,"E11.sketch_text.stroke-9"),sQuery(id+"F14.wireOp",EDGE,"E11.sketch_text.stroke-10"),sQuery(id+"F14.wireOp",EDGE,"E11.sketch_text.stroke-11"),sQuery(id+"F14.wireOp",EDGE,"E11.sketch_text.stroke-12"),sQuery(id+"F14.wireOp",EDGE,"E11.sketch_text.stroke-13"),sQuery(id+"F14.wireOp",EDGE,"E11.sketch_text.stroke-14")])]});
            var Q1;
            Q1=makeQuery(id+"F15.opExtrude","SWEPT_BODY",BODY,{"disambiguationData":[OSD([sQuery(id+"F14.wireOp",EDGE,"E11.sketch_text.stroke-15"),sQuery(id+"F14.wireOp",EDGE,"E11.sketch_text.stroke-16"),sQuery(id+"F14.wireOp",EDGE,"E11.sketch_text.stroke-17"),sQuery(id+"F14.wireOp",EDGE,"E11.sketch_text.stroke-18"),sQuery(id+"F14.wireOp",EDGE,"E11.sketch_text.stroke-19"),sQuery(id+"F14.wireOp",EDGE,"E11.sketch_text.stroke-20"),sQuery(id+"F14.wireOp",EDGE,"E11.sketch_text.stroke-21"),sQuery(id+"F14.wireOp",EDGE,"E11.sketch_text.stroke-22"),sQuery(id+"F14.wireOp",EDGE,"E11.sketch_text.stroke-23"),sQuery(id+"F14.wireOp",EDGE,"E11.sketch_text.stroke-24"),sQuery(id+"F14.wireOp",EDGE,"E11.sketch_text.stroke-25"),sQuery(id+"F14.wireOp",EDGE,"E11.sketch_text.stroke-26"),sQuery(id+"F14.wireOp",EDGE,"E11.sketch_text.stroke-27"),sQuery(id+"F14.wireOp",EDGE,"E11.sketch_text.stroke-28"),sQuery(id+"F14.wireOp",EDGE,"E11.sketch_text.stroke-29"),sQuery(id+"F14.wireOp",EDGE,"E11.sketch_text.stroke-30"),sQuery(id+"F14.wireOp",EDGE,"E11.sketch_text.stroke-31"),sQuery(id+"F14.wireOp",EDGE,"E11.sketch_text.stroke-32"),sQuery(id+"F14.wireOp",EDGE,"E11.sketch_text.stroke-33"),sQuery(id+"F14.wireOp",EDGE,"E11.sketch_text.stroke-34"),sQuery(id+"F14.wireOp",EDGE,"E11.sketch_text.stroke-35"),sQuery(id+"F14.wireOp",EDGE,"E11.sketch_text.stroke-36"),sQuery(id+"F14.wireOp",EDGE,"E11.sketch_text.stroke-37"),sQuery(id+"F14.wireOp",EDGE,"E11.sketch_text.stroke-38"),sQuery(id+"F14.wireOp",EDGE,"E11.sketch_text.stroke-39"),sQuery(id+"F14.wireOp",EDGE,"E11.sketch_text.stroke-40"),sQuery(id+"F14.wireOp",EDGE,"E11.sketch_text.stroke-41")])]});
            var Q2;
            Q2=makeQuery(id+"F15.opExtrude","SWEPT_BODY",BODY,{"disambiguationData":[OSD([sQuery(id+"F14.wireOp",EDGE,"E11.sketch_text.stroke-42"),sQuery(id+"F14.wireOp",EDGE,"E11.sketch_text.stroke-43"),sQuery(id+"F14.wireOp",EDGE,"E11.sketch_text.stroke-44"),sQuery(id+"F14.wireOp",EDGE,"E11.sketch_text.stroke-45"),sQuery(id+"F14.wireOp",EDGE,"E11.sketch_text.stroke-46"),sQuery(id+"F14.wireOp",EDGE,"E11.sketch_text.stroke-47"),sQuery(id+"F14.wireOp",EDGE,"E11.sketch_text.stroke-48"),sQuery(id+"F14.wireOp",EDGE,"E11.sketch_text.stroke-49"),sQuery(id+"F14.wireOp",EDGE,"E11.sketch_text.stroke-50"),sQuery(id+"F14.wireOp",EDGE,"E11.sketch_text.stroke-51"),sQuery(id+"F14.wireOp",EDGE,"E11.sketch_text.stroke-52"),sQuery(id+"F14.wireOp",EDGE,"E11.sketch_text.stroke-53"),sQuery(id+"F14.wireOp",EDGE,"E11.sketch_text.stroke-54")])]});
            var Q3;
            Q3=makeQuery(id+"F15.opExtrude","SWEPT_BODY",BODY,{"disambiguationData":[OSD([sQuery(id+"F14.wireOp",EDGE,"E11.sketch_text.stroke-55"),sQuery(id+"F14.wireOp",EDGE,"E11.sketch_text.stroke-56"),sQuery(id+"F14.wireOp",EDGE,"E11.sketch_text.stroke-57"),sQuery(id+"F14.wireOp",EDGE,"E11.sketch_text.stroke-58"),sQuery(id+"F14.wireOp",EDGE,"E11.sketch_text.stroke-59"),sQuery(id+"F14.wireOp",EDGE,"E11.sketch_text.stroke-60"),sQuery(id+"F14.wireOp",EDGE,"E11.sketch_text.stroke-61"),sQuery(id+"F14.wireOp",EDGE,"E11.sketch_text.stroke-62"),sQuery(id+"F14.wireOp",EDGE,"E11.sketch_text.stroke-63"),sQuery(id+"F14.wireOp",EDGE,"E11.sketch_text.stroke-64"),sQuery(id+"F14.wireOp",EDGE,"E11.sketch_text.stroke-65"),sQuery(id+"F14.wireOp",EDGE,"E11.sketch_text.stroke-66"),sQuery(id+"F14.wireOp",EDGE,"E11.sketch_text.stroke-67"),sQuery(id+"F14.wireOp",EDGE,"E11.sketch_text.stroke-68"),sQuery(id+"F14.wireOp",EDGE,"E11.sketch_text.stroke-69"),sQuery(id+"F14.wireOp",EDGE,"E11.sketch_text.stroke-70"),sQuery(id+"F14.wireOp",EDGE,"E11.sketch_text.stroke-71"),sQuery(id+"F14.wireOp",EDGE,"E11.sketch_text.stroke-72"),sQuery(id+"F14.wireOp",EDGE,"E11.sketch_text.stroke-73")])]});
            var Q4;
            Q4=makeQuery(id+"F15.opExtrude","SWEPT_BODY",BODY,{"disambiguationData":[OSD([sQuery(id+"F14.wireOp",EDGE,"E11.sketch_text.stroke-74"),sQuery(id+"F14.wireOp",EDGE,"E11.sketch_text.stroke-75"),sQuery(id+"F14.wireOp",EDGE,"E11.sketch_text.stroke-76"),sQuery(id+"F14.wireOp",EDGE,"E11.sketch_text.stroke-77")])]});
            var Q5;
            Q5=makeQuery(id+"F15.opExtrude","SWEPT_BODY",BODY,{"disambiguationData":[OSD([sQuery(id+"F14.wireOp",EDGE,"E11.sketch_text.stroke-78"),sQuery(id+"F14.wireOp",EDGE,"E11.sketch_text.stroke-79"),sQuery(id+"F14.wireOp",EDGE,"E11.sketch_text.stroke-80"),sQuery(id+"F14.wireOp",EDGE,"E11.sketch_text.stroke-81"),sQuery(id+"F14.wireOp",EDGE,"E11.sketch_text.stroke-82"),sQuery(id+"F14.wireOp",EDGE,"E11.sketch_text.stroke-83"),sQuery(id+"F14.wireOp",EDGE,"E11.sketch_text.stroke-84"),sQuery(id+"F14.wireOp",EDGE,"E11.sketch_text.stroke-85")])]});
            var Q6;
            Q6=makeQuery(id+"F15.opExtrude","SWEPT_BODY",BODY,{"disambiguationData":[OSD([sQuery(id+"F14.wireOp",EDGE,"E11.sketch_text.stroke-86"),sQuery(id+"F14.wireOp",EDGE,"E11.sketch_text.stroke-87"),sQuery(id+"F14.wireOp",EDGE,"E11.sketch_text.stroke-88"),sQuery(id+"F14.wireOp",EDGE,"E11.sketch_text.stroke-89"),sQuery(id+"F14.wireOp",EDGE,"E11.sketch_text.stroke-90"),sQuery(id+"F14.wireOp",EDGE,"E11.sketch_text.stroke-91"),sQuery(id+"F14.wireOp",EDGE,"E11.sketch_text.stroke-92"),sQuery(id+"F14.wireOp",EDGE,"E11.sketch_text.stroke-93"),sQuery(id+"F14.wireOp",EDGE,"E11.sketch_text.stroke-94"),sQuery(id+"F14.wireOp",EDGE,"E11.sketch_text.stroke-95"),sQuery(id+"F14.wireOp",EDGE,"E11.sketch_text.stroke-96"),sQuery(id+"F14.wireOp",EDGE,"E11.sketch_text.stroke-97"),sQuery(id+"F14.wireOp",EDGE,"E11.sketch_text.stroke-98"),sQuery(id+"F14.wireOp",EDGE,"E11.sketch_text.stroke-99"),sQuery(id+"F14.wireOp",EDGE,"E11.sketch_text.stroke-100")])]});
            var Q7;
            Q7=makeQuery(id+"F15.opExtrude","SWEPT_BODY",BODY,{"disambiguationData":[OSD([sQuery(id+"F14.wireOp",EDGE,"E11.sketch_text.stroke-101"),sQuery(id+"F14.wireOp",EDGE,"E11.sketch_text.stroke-102"),sQuery(id+"F14.wireOp",EDGE,"E11.sketch_text.stroke-103"),sQuery(id+"F14.wireOp",EDGE,"E11.sketch_text.stroke-104")])]});
            var Q8;
            Q8=makeQuery(id+"F15.opExtrude","SWEPT_BODY",BODY,{"disambiguationData":[OSD([sQuery(id+"F14.wireOp",EDGE,"E11.sketch_text.stroke-105"),sQuery(id+"F14.wireOp",EDGE,"E11.sketch_text.stroke-106"),sQuery(id+"F14.wireOp",EDGE,"E11.sketch_text.stroke-107"),sQuery(id+"F14.wireOp",EDGE,"E11.sketch_text.stroke-108"),sQuery(id+"F14.wireOp",EDGE,"E11.sketch_text.stroke-109"),sQuery(id+"F14.wireOp",EDGE,"E11.sketch_text.stroke-110"),sQuery(id+"F14.wireOp",EDGE,"E11.sketch_text.stroke-111"),sQuery(id+"F14.wireOp",EDGE,"E11.sketch_text.stroke-112"),sQuery(id+"F14.wireOp",EDGE,"E11.sketch_text.stroke-113"),sQuery(id+"F14.wireOp",EDGE,"E11.sketch_text.stroke-114"),sQuery(id+"F14.wireOp",EDGE,"E11.sketch_text.stroke-115"),sQuery(id+"F14.wireOp",EDGE,"E11.sketch_text.stroke-116"),sQuery(id+"F14.wireOp",EDGE,"E11.sketch_text.stroke-117"),sQuery(id+"F14.wireOp",EDGE,"E11.sketch_text.stroke-118"),sQuery(id+"F14.wireOp",EDGE,"E11.sketch_text.stroke-119"),sQuery(id+"F14.wireOp",EDGE,"E11.sketch_text.stroke-120"),sQuery(id+"F14.wireOp",EDGE,"E11.sketch_text.stroke-121"),sQuery(id+"F14.wireOp",EDGE,"E11.sketch_text.stroke-122"),sQuery(id+"F14.wireOp",EDGE,"E11.sketch_text.stroke-123")])]});
            var Q9;
            Q9=makeQuery(id+"F15.opExtrude","SWEPT_BODY",BODY,{"disambiguationData":[OSD([sQuery(id+"F14.wireOp",EDGE,"E11.sketch_text.stroke-124"),sQuery(id+"F14.wireOp",EDGE,"E11.sketch_text.stroke-125"),sQuery(id+"F14.wireOp",EDGE,"E11.sketch_text.stroke-126"),sQuery(id+"F14.wireOp",EDGE,"E11.sketch_text.stroke-127"),sQuery(id+"F14.wireOp",EDGE,"E11.sketch_text.stroke-128"),sQuery(id+"F14.wireOp",EDGE,"E11.sketch_text.stroke-129"),sQuery(id+"F14.wireOp",EDGE,"E11.sketch_text.stroke-130"),sQuery(id+"F14.wireOp",EDGE,"E11.sketch_text.stroke-131"),sQuery(id+"F14.wireOp",EDGE,"E11.sketch_text.stroke-132"),sQuery(id+"F14.wireOp",EDGE,"E11.sketch_text.stroke-133"),sQuery(id+"F14.wireOp",EDGE,"E11.sketch_text.stroke-134"),sQuery(id+"F14.wireOp",EDGE,"E11.sketch_text.stroke-135"),sQuery(id+"F14.wireOp",EDGE,"E11.sketch_text.stroke-136"),sQuery(id+"F14.wireOp",EDGE,"E11.sketch_text.stroke-137"),sQuery(id+"F14.wireOp",EDGE,"E11.sketch_text.stroke-138")])]});
            var Q10;
            Q10=makeQuery(id+"F15.opExtrude","SWEPT_BODY",BODY,{"disambiguationData":[OSD([sQuery(id+"F14.wireOp",EDGE,"E11.sketch_text.stroke-139"),sQuery(id+"F14.wireOp",EDGE,"E11.sketch_text.stroke-140"),sQuery(id+"F14.wireOp",EDGE,"E11.sketch_text.stroke-141"),sQuery(id+"F14.wireOp",EDGE,"E11.sketch_text.stroke-142"),sQuery(id+"F14.wireOp",EDGE,"E11.sketch_text.stroke-143"),sQuery(id+"F14.wireOp",EDGE,"E11.sketch_text.stroke-144"),sQuery(id+"F14.wireOp",EDGE,"E11.sketch_text.stroke-145"),sQuery(id+"F14.wireOp",EDGE,"E11.sketch_text.stroke-146"),sQuery(id+"F14.wireOp",EDGE,"E11.sketch_text.stroke-147"),sQuery(id+"F14.wireOp",EDGE,"E11.sketch_text.stroke-148"),sQuery(id+"F14.wireOp",EDGE,"E11.sketch_text.stroke-149"),sQuery(id+"F14.wireOp",EDGE,"E11.sketch_text.stroke-150"),sQuery(id+"F14.wireOp",EDGE,"E11.sketch_text.stroke-151"),sQuery(id+"F14.wireOp",EDGE,"E11.sketch_text.stroke-152"),sQuery(id+"F14.wireOp",EDGE,"E11.sketch_text.stroke-153"),sQuery(id+"F14.wireOp",EDGE,"E11.sketch_text.stroke-154"),sQuery(id+"F14.wireOp",EDGE,"E11.sketch_text.stroke-155"),sQuery(id+"F14.wireOp",EDGE,"E11.sketch_text.stroke-156")])]});
            var Q11;
            Q11=makeQuery(id+"F15.opExtrude","SWEPT_BODY",BODY,{"disambiguationData":[OSD([sQuery(id+"F14.wireOp",EDGE,"E11.sketch_text.stroke-157"),sQuery(id+"F14.wireOp",EDGE,"E11.sketch_text.stroke-158"),sQuery(id+"F14.wireOp",EDGE,"E11.sketch_text.stroke-159"),sQuery(id+"F14.wireOp",EDGE,"E11.sketch_text.stroke-160"),sQuery(id+"F14.wireOp",EDGE,"E11.sketch_text.stroke-161"),sQuery(id+"F14.wireOp",EDGE,"E11.sketch_text.stroke-162"),sQuery(id+"F14.wireOp",EDGE,"E11.sketch_text.stroke-163"),sQuery(id+"F14.wireOp",EDGE,"E11.sketch_text.stroke-164"),sQuery(id+"F14.wireOp",EDGE,"E11.sketch_text.stroke-165"),sQuery(id+"F14.wireOp",EDGE,"E11.sketch_text.stroke-166"),sQuery(id+"F14.wireOp",EDGE,"E11.sketch_text.stroke-167"),sQuery(id+"F14.wireOp",EDGE,"E11.sketch_text.stroke-168"),sQuery(id+"F14.wireOp",EDGE,"E11.sketch_text.stroke-169"),sQuery(id+"F14.wireOp",EDGE,"E11.sketch_text.stroke-170"),sQuery(id+"F14.wireOp",EDGE,"E11.sketch_text.stroke-171"),sQuery(id+"F14.wireOp",EDGE,"E11.sketch_text.stroke-172")])]});
            var Q12;
            Q12=makeQuery(id+"F15.opExtrude","SWEPT_BODY",BODY,{"disambiguationData":[OSD([sQuery(id+"F14.wireOp",EDGE,"E11.sketch_text.stroke-173"),sQuery(id+"F14.wireOp",EDGE,"E11.sketch_text.stroke-174"),sQuery(id+"F14.wireOp",EDGE,"E11.sketch_text.stroke-175"),sQuery(id+"F14.wireOp",EDGE,"E11.sketch_text.stroke-176"),sQuery(id+"F14.wireOp",EDGE,"E11.sketch_text.stroke-177"),sQuery(id+"F14.wireOp",EDGE,"E11.sketch_text.stroke-178"),sQuery(id+"F14.wireOp",EDGE,"E11.sketch_text.stroke-179"),sQuery(id+"F14.wireOp",EDGE,"E11.sketch_text.stroke-180"),sQuery(id+"F14.wireOp",EDGE,"E11.sketch_text.stroke-181"),sQuery(id+"F14.wireOp",EDGE,"E11.sketch_text.stroke-182"),sQuery(id+"F14.wireOp",EDGE,"E11.sketch_text.stroke-183"),sQuery(id+"F14.wireOp",EDGE,"E11.sketch_text.stroke-184"),sQuery(id+"F14.wireOp",EDGE,"E11.sketch_text.stroke-185"),sQuery(id+"F14.wireOp",EDGE,"E11.sketch_text.stroke-186"),sQuery(id+"F14.wireOp",EDGE,"E11.sketch_text.stroke-187"),sQuery(id+"F14.wireOp",EDGE,"E11.sketch_text.stroke-188"),sQuery(id+"F14.wireOp",EDGE,"E11.sketch_text.stroke-189"),sQuery(id+"F14.wireOp",EDGE,"E11.sketch_text.stroke-190"),sQuery(id+"F14.wireOp",EDGE,"E11.sketch_text.stroke-191"),sQuery(id+"F14.wireOp",EDGE,"E11.sketch_text.stroke-192"),sQuery(id+"F14.wireOp",EDGE,"E11.sketch_text.stroke-193"),sQuery(id+"F14.wireOp",EDGE,"E11.sketch_text.stroke-194"),sQuery(id+"F14.wireOp",EDGE,"E11.sketch_text.stroke-195"),sQuery(id+"F14.wireOp",EDGE,"E11.sketch_text.stroke-196"),sQuery(id+"F14.wireOp",EDGE,"E11.sketch_text.stroke-197")])]});
            var Q13;
            Q13=makeQuery(id+"F15.opExtrude","SWEPT_BODY",BODY,{"disambiguationData":[OSD([sQuery(id+"F14.wireOp",EDGE,"E11.sketch_text.stroke-198"),sQuery(id+"F14.wireOp",EDGE,"E11.sketch_text.stroke-199"),sQuery(id+"F14.wireOp",EDGE,"E11.sketch_text.stroke-200"),sQuery(id+"F14.wireOp",EDGE,"E11.sketch_text.stroke-201")])]});
            var Q14;
            Q14=makeQuery(id+"F15.opExtrude","SWEPT_BODY",BODY,{"disambiguationData":[OSD([sQuery(id+"F14.wireOp",EDGE,"E11.sketch_text.stroke-202"),sQuery(id+"F14.wireOp",EDGE,"E11.sketch_text.stroke-203"),sQuery(id+"F14.wireOp",EDGE,"E11.sketch_text.stroke-204"),sQuery(id+"F14.wireOp",EDGE,"E11.sketch_text.stroke-205"),sQuery(id+"F14.wireOp",EDGE,"E11.sketch_text.stroke-206"),sQuery(id+"F14.wireOp",EDGE,"E11.sketch_text.stroke-207"),sQuery(id+"F14.wireOp",EDGE,"E11.sketch_text.stroke-208"),sQuery(id+"F14.wireOp",EDGE,"E11.sketch_text.stroke-209")])]});
            var Q15;
            Q15=makeQuery(id+"F15.opExtrude","SWEPT_BODY",BODY,{"disambiguationData":[OSD([sQuery(id+"F14.wireOp",EDGE,"E11.sketch_text.stroke-210"),sQuery(id+"F14.wireOp",EDGE,"E11.sketch_text.stroke-211"),sQuery(id+"F14.wireOp",EDGE,"E11.sketch_text.stroke-212"),sQuery(id+"F14.wireOp",EDGE,"E11.sketch_text.stroke-213"),sQuery(id+"F14.wireOp",EDGE,"E11.sketch_text.stroke-214"),sQuery(id+"F14.wireOp",EDGE,"E11.sketch_text.stroke-215"),sQuery(id+"F14.wireOp",EDGE,"E11.sketch_text.stroke-216"),sQuery(id+"F14.wireOp",EDGE,"E11.sketch_text.stroke-217"),sQuery(id+"F14.wireOp",EDGE,"E11.sketch_text.stroke-218"),sQuery(id+"F14.wireOp",EDGE,"E11.sketch_text.stroke-219"),sQuery(id+"F14.wireOp",EDGE,"E11.sketch_text.stroke-220"),sQuery(id+"F14.wireOp",EDGE,"E11.sketch_text.stroke-221"),sQuery(id+"F14.wireOp",EDGE,"E11.sketch_text.stroke-222"),sQuery(id+"F14.wireOp",EDGE,"E11.sketch_text.stroke-223"),sQuery(id+"F14.wireOp",EDGE,"E11.sketch_text.stroke-224")])]});
            var Q16;
            Q16=makeQuery(id+"F15.opExtrude","SWEPT_BODY",BODY,{"disambiguationData":[OSD([sQuery(id+"F14.wireOp",EDGE,"E11.sketch_text.stroke-225"),sQuery(id+"F14.wireOp",EDGE,"E11.sketch_text.stroke-226"),sQuery(id+"F14.wireOp",EDGE,"E11.sketch_text.stroke-227"),sQuery(id+"F14.wireOp",EDGE,"E11.sketch_text.stroke-228"),sQuery(id+"F14.wireOp",EDGE,"E11.sketch_text.stroke-229"),sQuery(id+"F14.wireOp",EDGE,"E11.sketch_text.stroke-230"),sQuery(id+"F14.wireOp",EDGE,"E11.sketch_text.stroke-231"),sQuery(id+"F14.wireOp",EDGE,"E11.sketch_text.stroke-232"),sQuery(id+"F14.wireOp",EDGE,"E11.sketch_text.stroke-233"),sQuery(id+"F14.wireOp",EDGE,"E11.sketch_text.stroke-234"),sQuery(id+"F14.wireOp",EDGE,"E11.sketch_text.stroke-235"),sQuery(id+"F14.wireOp",EDGE,"E11.sketch_text.stroke-236"),sQuery(id+"F14.wireOp",EDGE,"E11.sketch_text.stroke-237"),sQuery(id+"F14.wireOp",EDGE,"E11.sketch_text.stroke-238"),sQuery(id+"F14.wireOp",EDGE,"E11.sketch_text.stroke-239"),sQuery(id+"F14.wireOp",EDGE,"E11.sketch_text.stroke-240"),sQuery(id+"F14.wireOp",EDGE,"E11.sketch_text.stroke-241"),sQuery(id+"F14.wireOp",EDGE,"E11.sketch_text.stroke-242"),sQuery(id+"F14.wireOp",EDGE,"E11.sketch_text.stroke-243"),sQuery(id+"F14.wireOp",EDGE,"E11.sketch_text.stroke-244"),sQuery(id+"F14.wireOp",EDGE,"E11.sketch_text.stroke-245"),sQuery(id+"F14.wireOp",EDGE,"E11.sketch_text.stroke-246"),sQuery(id+"F14.wireOp",EDGE,"E11.sketch_text.stroke-247"),sQuery(id+"F14.wireOp",EDGE,"E11.sketch_text.stroke-248"),sQuery(id+"F14.wireOp",EDGE,"E11.sketch_text.stroke-249")])]});
            transform(context, id + "F18", {"entities" : qUnion([Q0, Q1, Q2, Q3, Q4, Q5, Q6, Q7, Q8, Q9, Q10, Q11, Q12, Q13, Q14, Q15, Q16]), "transformType" : TransformType.TRANSLATION_3D, "dx" : 3.1 * mm, "dy" : -14.3 * mm, "dz" : -0.9 * mm, "makeCopy" : false});
        }
        {
            var Q0;
            Q0=makeQuery(id+"F15.opExtrude","SWEPT_BODY",BODY,{"disambiguationData":[OSD([sQuery(id+"F14.wireOp",EDGE,"E9.sketch_text.stroke-104"),sQuery(id+"F14.wireOp",EDGE,"E9.sketch_text.stroke-105"),sQuery(id+"F14.wireOp",EDGE,"E9.sketch_text.stroke-106"),sQuery(id+"F14.wireOp",EDGE,"E9.sketch_text.stroke-107"),sQuery(id+"F14.wireOp",EDGE,"E9.sketch_text.stroke-108"),sQuery(id+"F14.wireOp",EDGE,"E9.sketch_text.stroke-109"),sQuery(id+"F14.wireOp",EDGE,"E9.sketch_text.stroke-110"),sQuery(id+"F14.wireOp",EDGE,"E9.sketch_text.stroke-111"),sQuery(id+"F14.wireOp",EDGE,"E9.sketch_text.stroke-112"),sQuery(id+"F14.wireOp",EDGE,"E9.sketch_text.stroke-113"),sQuery(id+"F14.wireOp",EDGE,"E9.sketch_text.stroke-114"),sQuery(id+"F14.wireOp",EDGE,"E9.sketch_text.stroke-115"),sQuery(id+"F14.wireOp",EDGE,"E9.sketch_text.stroke-116"),sQuery(id+"F14.wireOp",EDGE,"E9.sketch_text.stroke-117"),sQuery(id+"F14.wireOp",EDGE,"E9.sketch_text.stroke-118"),sQuery(id+"F14.wireOp",EDGE,"E9.sketch_text.stroke-119"),sQuery(id+"F14.wireOp",EDGE,"E9.sketch_text.stroke-120")])]});
            transform(context, id + "F19", {"entities" : qUnion([Q0]), "transformType" : TransformType.TRANSLATION_3D, "dx" : -49.2 * mm, "dy" : -33.1 * mm, "dz" : -18 * mm, "makeCopy" : true});
        }
    });